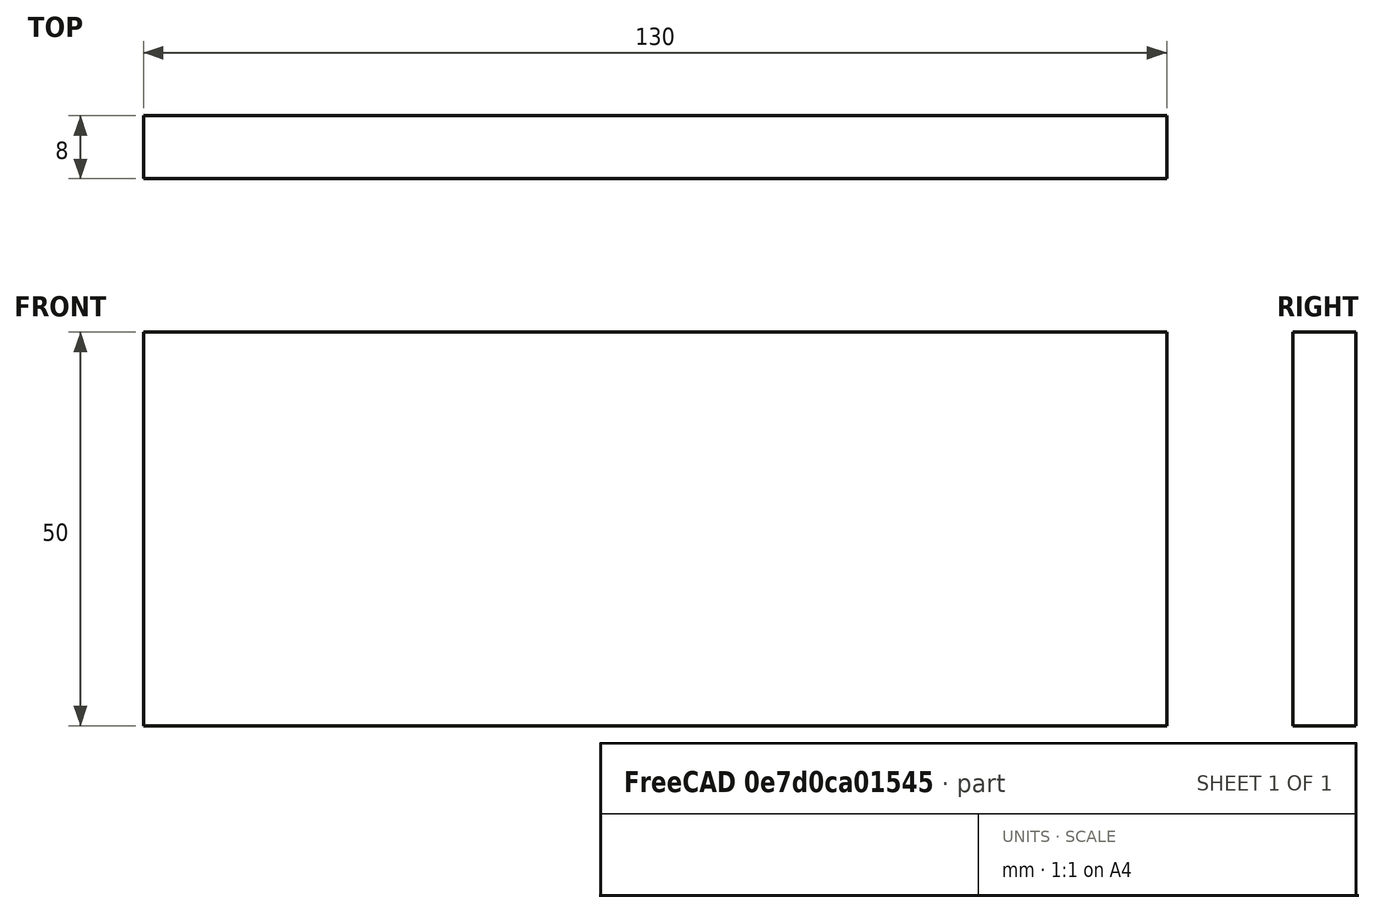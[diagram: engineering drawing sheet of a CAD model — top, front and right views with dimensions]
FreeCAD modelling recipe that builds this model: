
FCSTD DOCUMENT  (FreeCAD 0.15R4671 (Git))
Label: Flat Bar 130x8 EN10058 S235JR
License: All rights reserved
LicenseURL: http://en.wikipedia.org/wiki/All_rights_reserved
objects: Sketcher::SketchObject×1, Part::Extrusion×1
note: 2 computed .brp shape members not serialized (recipe doc carries the construction recipe); baked Part::Feature solids carry a one-line shape summary decoded from their .brp

FEATURE [Sketcher::SketchObject] Sketch
  sketch-geometry (4):
    g0: LineSegment StartX=-65 StartY=-4 StartZ=0 EndX=65 EndY=-4 EndZ=0
    g1: LineSegment StartX=65 StartY=-4 StartZ=0 EndX=65 EndY=4 EndZ=0
    g2: LineSegment StartX=65 StartY=4 StartZ=0 EndX=-65 EndY=4 EndZ=0
    g3: LineSegment StartX=-65 StartY=4 StartZ=0 EndX=-65 EndY=-4 EndZ=0
  constraints (12):
    c: Coincident(g0,g1)
    c: Coincident(g1,g2)
    c: Coincident(g2,g3)
    c: Coincident(g3,g0)
    c: Horizontal(g0)
    c: Horizontal(g2)
    c: Vertical(g1)
    c: Vertical(g3)
    c: Symmetric(g1,g2,g-2)
    c: Symmetric(g0,g1,g-1)
    c: DistanceY(g1) = 8
    c: DistanceX(g0) = 130
FEATURE [Part::Extrusion] Extrude  label="Flat Bar 130x8 EN10058 S235JR"
  Base = -> Sketch
  Dir = (0,0,50)
  Solid = true
